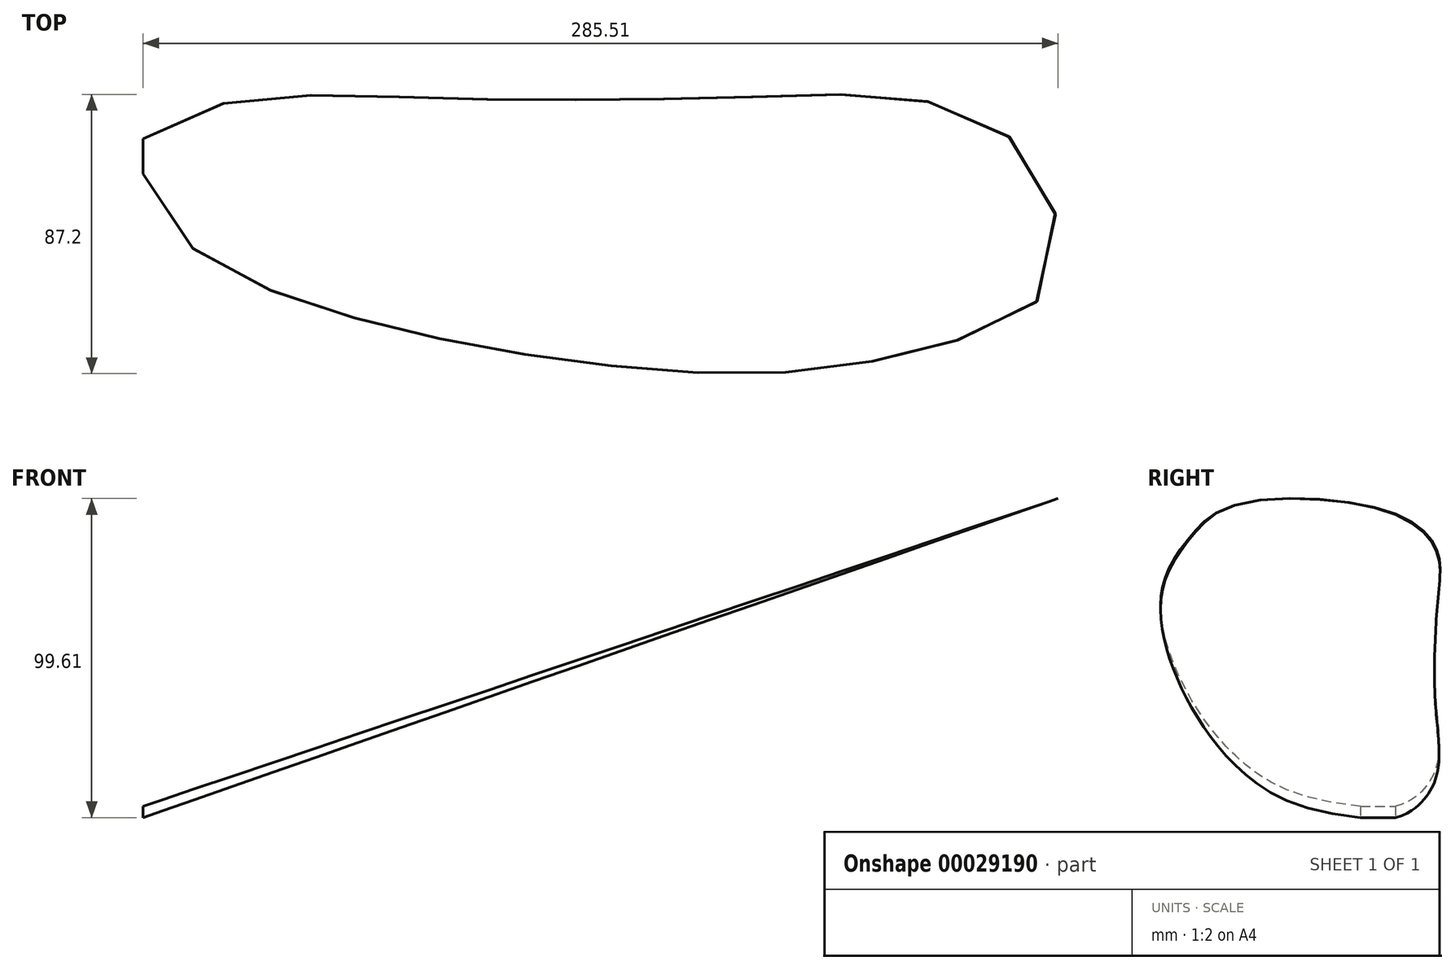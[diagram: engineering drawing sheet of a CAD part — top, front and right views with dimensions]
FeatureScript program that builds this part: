
annotation { "Feature Type Name" : "Feature", "Feature Type Description" : "" }
export const myFeature = defineFeature(function(context is Context, id is Id, definition is map)
    precondition{}
    {
        {
            var Q0;
            Q0=qCreatedBy(makeId("Front.planeOp"),FACE);
            var sketch = newSketch(context, id + "F0", { "sketchPlane" : qUnion([Q0])});
            skLineSegment(sketch, "E0", {"start": v(0, 0) * mm, "end": v(0, 50) * mm, "construction": true});
            skLineSegment(sketch, "E1", {"start": v(0, 50) * mm, "end": v(0, 53.54) * mm});
            skLineSegment(sketch, "E2", {"start": v(0, 53.54) * mm, "end": v(285.78, 149.7) * mm});
            skLineSegment(sketch, "E3", {"start": v(285.78, 149.7) * mm, "end": v(0, 50) * mm});
            skSolve(sketch);
        }
        {
            var Q0;
            Q0 = qSketchRegion(id + "F0", true);
            extrude(context, id + "F1", {"entities" : qUnion([Q0]), "endBound" : BoundingType.SYMMETRIC, "depth" : 100 * mm});
        }
        {
            var Q0;
            Q0=qCreatedBy(makeId("Top.planeOp"),FACE);
            var sketch = newSketch(context, id + "F2", { "sketchPlane" : qUnion([Q0])});
            skLineSegment(sketch, "E4", {"start": v(0, 0) * mm, "end": v(-177.05, 0) * mm, "construction": true});
            skLineSegment(sketch, "E5", {"start": v(29.18, 42.2) * mm, "end": v(239.56, 44.18) * mm, "construction": true});
            skLineSegment(sketch, "E6", {"start": v(24.9, -4.98) * mm, "end": v(231.51, -44.72) * mm, "construction": true});
            skArc(sketch, "E7", {"start": v(231.51, -44.72) * mm, "mid": v(284.65, -4.72) * mm, "end": v(239.56, 44.18) * mm, "construction": true});
            skArc(sketch, "E8", {"start": v(29.18, 42.2) * mm, "mid": v(5.7, 20.54) * mm, "end": v(24.9, -4.98) * mm, "construction": true});
            skLineSegment(sketch, "E9.bottom", {"start": v(-12.02, 61.92) * mm, "end": v(299.08, 61.92) * mm});
            skLineSegment(sketch, "E9.top", {"start": v(-12.02, -60.76) * mm, "end": v(299.08, -60.76) * mm});
            skLineSegment(sketch, "E9.left", {"start": v(-12.02, 61.92) * mm, "end": v(-12.02, -60.76) * mm});
            skLineSegment(sketch, "E9.right", {"start": v(299.08, 61.92) * mm, "end": v(299.08, -60.76) * mm});
            skFitSpline(sketch, "E10", {"points": [v(29.18, 42.2) * mm, v(101.43, 42.87) * mm, v(199.86, 43.8) * mm, v(244.38, 42.2) * mm, v(278.44, 22.4) * mm, v(282.1, -16.12) * mm, v(250.51, -33.45) * mm, v(179.2, -42.8) * mm, v(20.44, -7.31) * mm, v(0, 19.47) * mm, v(0, 30.44) * mm, v(29.18, 42.2) * mm]});
            skSolve(sketch);
        }
        {
            var Q0;
            Q0 = qSketchRegion(id + "F2", true);
            extrude(context, id + "F3", {"entities" : qUnion([Q0]), "operationType" : NewBodyOperationType.REMOVE, "depth" : 200 * mm});
        }
    });
